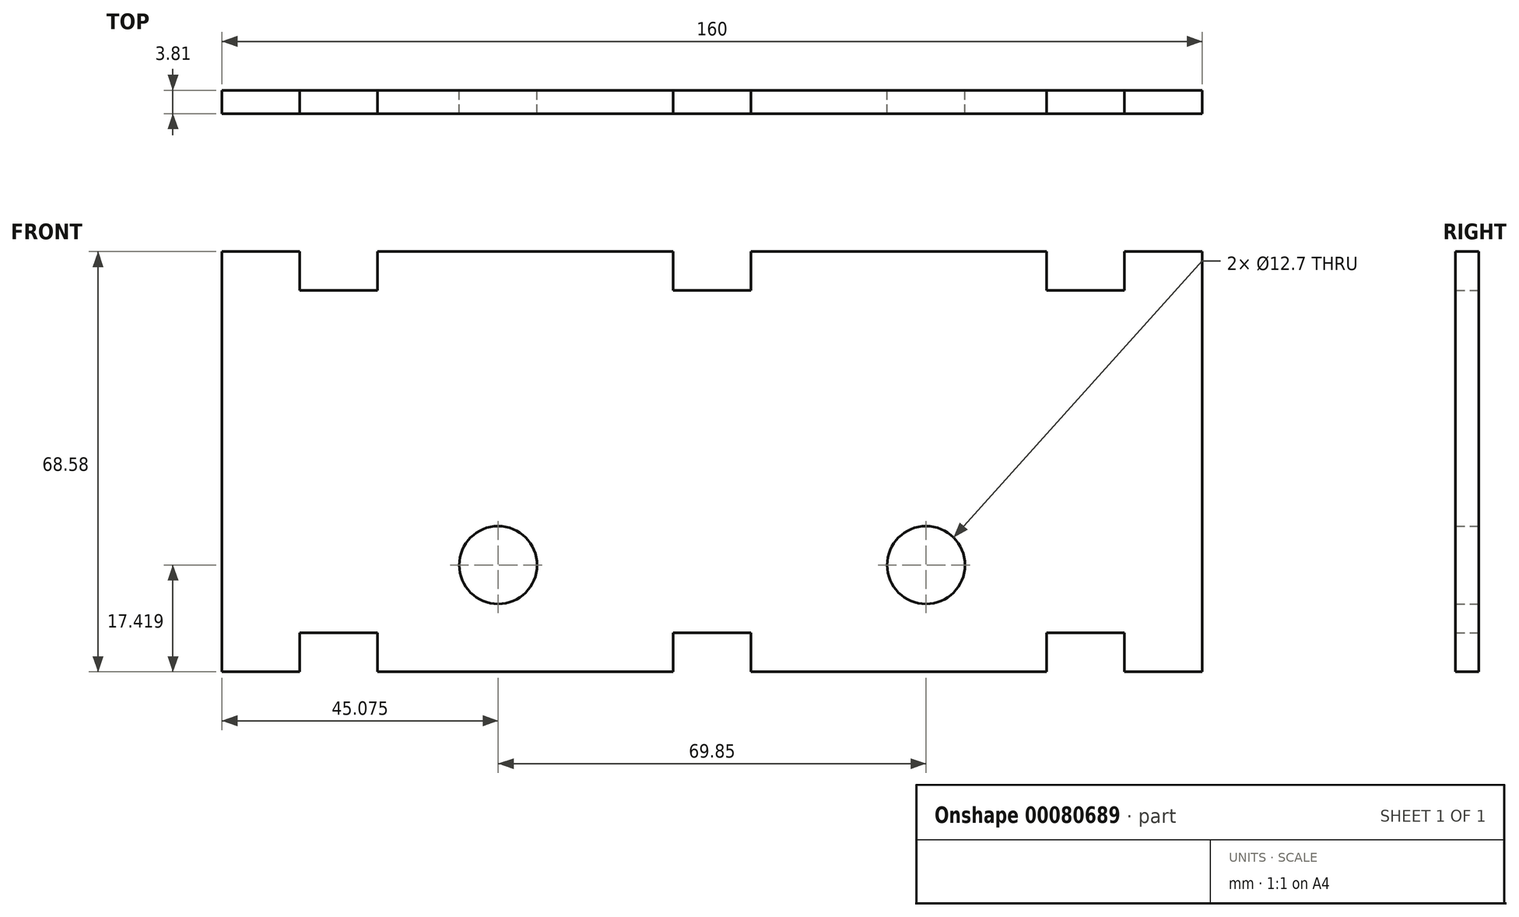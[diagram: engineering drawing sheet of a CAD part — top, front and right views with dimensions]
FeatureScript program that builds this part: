
annotation { "Feature Type Name" : "Feature", "Feature Type Description" : "" }
export const myFeature = defineFeature(function(context is Context, id is Id, definition is map)
    precondition{}
    {
        {
            var Q0;
            Q0=qCreatedBy(makeId("Front.planeOp"),FACE);
            var sketch = newSketch(context, id + "F0", { "sketchPlane" : qUnion([Q0])});
            skLineSegment(sketch, "E0.top", {"start": v(-80, -34.3) * mm, "end": v(-67.3, -34.3) * mm});
            skLineSegment(sketch, "E0.left", {"start": v(-80, 34.3) * mm, "end": v(-80, -34.3) * mm});
            skLineSegment(sketch, "E0.right", {"start": v(80, 34.3) * mm, "end": v(80, -34.3) * mm});
            skPoint(sketch, "E0.middle", {"position": v(0, 0) * mm});
            skPoint(sketch, "E1.middle", {"position": v(-60.95, 34.3) * mm});
            skPoint(sketch, "E2.middle", {"position": v(60.95, 34.3) * mm});
            skLineSegment(sketch, "E3.left", {"start": v(-6.35, 34.3) * mm, "end": v(-6.35, 27.94) * mm});
            skPoint(sketch, "E3.middle", {"position": v(0, 34.3) * mm});
            skLineSegment(sketch, "E4.MirrorCS", {"start": v(-6.35, -34.3) * mm, "end": v(-6.35, -27.94) * mm});
            skLineSegment(sketch, "E5.MirrorCS", {"start": v(-6.35, -27.94) * mm, "end": v(6.35, -27.94) * mm});
            skLineSegment(sketch, "E6.MirrorCS", {"start": v(6.35, -34.3) * mm, "end": v(6.35, -27.94) * mm});
            skLineSegment(sketch, "E7.MirrorCS", {"start": v(54.6, -27.94) * mm, "end": v(67.3, -27.94) * mm});
            skLineSegment(sketch, "E8.MirrorCS", {"start": v(54.6, -34.3) * mm, "end": v(54.6, -27.94) * mm});
            skLineSegment(sketch, "E9.MirrorCS", {"start": v(67.3, -34.3) * mm, "end": v(67.3, -27.94) * mm});
            skLineSegment(sketch, "E10.MirrorCS", {"start": v(-54.6, -34.3) * mm, "end": v(-54.6, -27.94) * mm});
            skLineSegment(sketch, "E11.MirrorCS", {"start": v(-67.3, -27.94) * mm, "end": v(-54.6, -27.94) * mm});
            skLineSegment(sketch, "E12.MirrorCS", {"start": v(-67.3, -34.3) * mm, "end": v(-67.3, -27.94) * mm});
            skPoint(sketch, "E13.orphan", {"position": v(-67.3, 40.64) * mm});
            skPoint(sketch, "E14.orphan", {"position": v(-6.35, 40.64) * mm});
            skPoint(sketch, "E15.orphan", {"position": v(6.35, 40.64) * mm});
            skPoint(sketch, "E2.bottom.start.orphan", {"position": v(54.6, 40.64) * mm});
            skPoint(sketch, "E16.orphan", {"position": v(67.3, 40.64) * mm});
            skPoint(sketch, "E17.orphan", {"position": v(54.6, -40.64) * mm});
            skPoint(sketch, "E18.orphan", {"position": v(67.3, -40.64) * mm});
            skPoint(sketch, "E19.orphan", {"position": v(6.35, -40.64) * mm});
            skPoint(sketch, "E20.orphan", {"position": v(-6.35, -40.64) * mm});
            skPoint(sketch, "E21.orphan", {"position": v(-54.6, -40.64) * mm});
            skPoint(sketch, "E22.orphan", {"position": v(-67.3, -40.64) * mm});
            skLineSegment(sketch, "E23.trimOffspring", {"start": v(-54.6, -34.3) * mm, "end": v(-6.35, -34.3) * mm});
            skLineSegment(sketch, "E24.trimOffspring", {"start": v(6.35, -34.3) * mm, "end": v(54.6, -34.3) * mm});
            skLineSegment(sketch, "E25.trimOffspring", {"start": v(67.3, -34.3) * mm, "end": v(80, -34.3) * mm});
            skCircle(sketch, "E26", {"center": v(-34.92, -16.87) * mm, "radius": 6.35 * mm});
            skCircle(sketch, "E27.MirrorC", {"center": v(34.92, -16.87) * mm, "radius": 6.35 * mm});
            skPoint(sketch, "E1.top.start.orphan", {"position": v(-67.3, 27.94) * mm});
            skPoint(sketch, "E1.right.end.orphan", {"position": v(-54.6, 27.94) * mm});
            skPoint(sketch, "E3.right.end.orphan", {"position": v(6.35, 27.94) * mm});
            skPoint(sketch, "E2.top.start.orphan", {"position": v(54.6, 27.94) * mm});
            skPoint(sketch, "E2.right.end.orphan", {"position": v(67.3, 27.94) * mm});
            skLineSegment(sketch, "E28.MirrorCS", {"start": v(-54.6, 34.3) * mm, "end": v(-6.35, 34.3) * mm});
            skLineSegment(sketch, "E29.MirrorCS", {"start": v(-67.3, 27.94) * mm, "end": v(-54.6, 27.94) * mm});
            skLineSegment(sketch, "E30.MirrorCS", {"start": v(-54.6, 34.3) * mm, "end": v(-54.6, 27.94) * mm});
            skLineSegment(sketch, "E31.MirrorCS", {"start": v(-67.3, 34.3) * mm, "end": v(-67.3, 27.94) * mm});
            skLineSegment(sketch, "E32.MirrorCS", {"start": v(-80, 34.3) * mm, "end": v(-67.3, 34.3) * mm});
            skLineSegment(sketch, "E33.MirrorCS", {"start": v(-6.35, 27.94) * mm, "end": v(6.35, 27.94) * mm});
            skLineSegment(sketch, "E34.MirrorCS", {"start": v(6.35, 34.3) * mm, "end": v(6.35, 27.94) * mm});
            skLineSegment(sketch, "E35.MirrorCS", {"start": v(6.35, 34.3) * mm, "end": v(54.6, 34.3) * mm});
            skLineSegment(sketch, "E36.MirrorCS", {"start": v(54.6, 34.3) * mm, "end": v(54.6, 27.94) * mm});
            skLineSegment(sketch, "E37.MirrorCS", {"start": v(54.6, 27.94) * mm, "end": v(67.3, 27.94) * mm});
            skLineSegment(sketch, "E38.MirrorCS", {"start": v(67.3, 34.3) * mm, "end": v(67.3, 27.94) * mm});
            skLineSegment(sketch, "E39.MirrorCS", {"start": v(67.3, 34.3) * mm, "end": v(80, 34.3) * mm});
            skSolve(sketch);
        }
        {
            var Q0;
            Q0=makeQuery(id+"F0.imprint","IMPRINT",FACE,{"disambiguationData":[TD([[makeQuery(id+"F0.imprint","IMPRINT",EDGE,{"derivedFrom":sQuery(id+"F0.wireOp",EDGE,"E0.bottom")}),-1.0]])]});
            var Q1;
            Q1=makeQuery(id+"F0.imprint","IMPRINT",FACE,{"disambiguationData":[TD([[makeQuery(id+"F0.imprint","IMPRINT",EDGE,{"derivedFrom":sQuery(id+"F0.wireOp",EDGE,"E0.top")}),1.0]])]});
            extrude(context, id + "F1", {"entities" : qUnion([Q0, Q1]), "depth" : 3.8 * mm});
        }
    });
